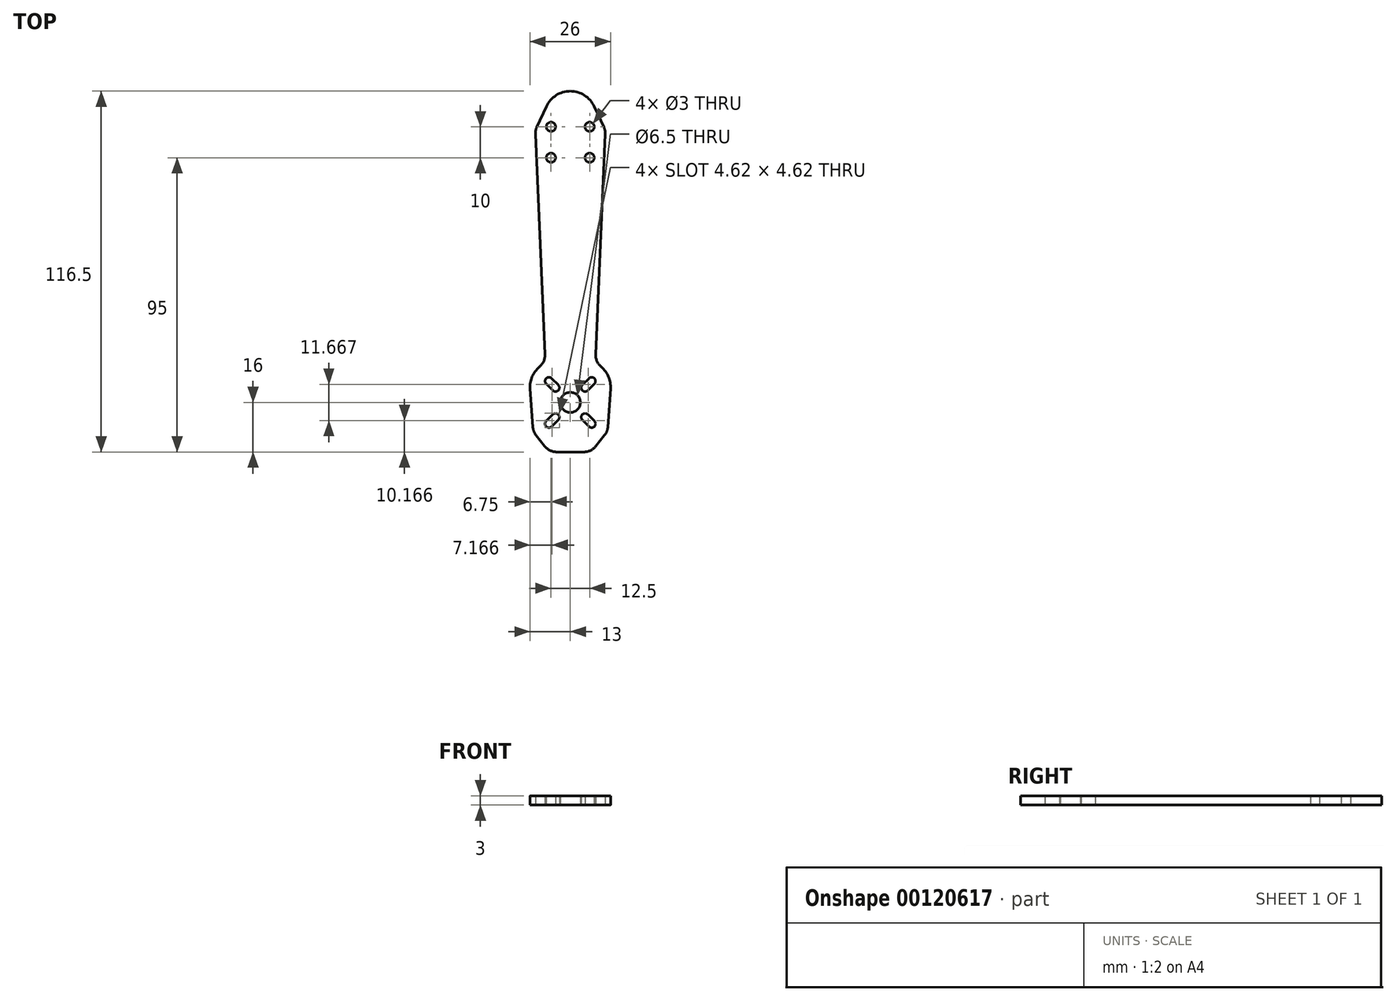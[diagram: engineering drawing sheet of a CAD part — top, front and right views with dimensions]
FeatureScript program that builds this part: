
annotation { "Feature Type Name" : "Feature", "Feature Type Description" : "" }
export const myFeature = defineFeature(function(context is Context, id is Id, definition is map)
    precondition{}
    {
        {
            var Q0;
            Q0=qCreatedBy(makeId("Top.planeOp"),FACE);
            var sketch = newSketch(context, id + "F0", { "sketchPlane" : qUnion([Q0])});
            skLineSegment(sketch, "E0", {"start": v(-6.01, -50.03) * mm, "end": v(-3.89, -47.9) * mm});
            skArc(sketch, "E1", {"start": v(-7.78, -48.26) * mm, "mid": v(-7.78, -50.03) * mm, "end": v(-6.01, -50.03) * mm});
            skArc(sketch, "E2", {"start": v(5.66, -46.14) * mm, "mid": v(3.89, -46.14) * mm, "end": v(3.89, -47.9) * mm});
            skArc(sketch, "E3", {"start": v(3.89, -36.6) * mm, "mid": v(3.89, -38.36) * mm, "end": v(5.66, -38.36) * mm});
            skArc(sketch, "E4", {"start": v(-6.01, -34.47) * mm, "mid": v(-7.78, -34.47) * mm, "end": v(-7.78, -36.24) * mm});
            skArc(sketch, "E5", {"start": v(11.28, 44.33) * mm, "mid": v(11.2, 45.52) * mm, "end": v(10.82, 46.66) * mm});
            skArc(sketch, "E6", {"start": v(12.98, -37.84) * mm, "mid": v(12.32, -33.93) * mm, "end": v(9.96, -30.74) * mm});
            skArc(sketch, "E7", {"start": v(-9.96, -30.74) * mm, "mid": v(-8.6, -28.92) * mm, "end": v(-8.18, -26.69) * mm});
            skArc(sketch, "E8", {"start": v(-9.96, -30.74) * mm, "mid": v(-12.32, -33.93) * mm, "end": v(-12.98, -37.84) * mm});
            skArc(sketch, "E9", {"start": v(8.18, -26.69) * mm, "mid": v(8.6, -28.92) * mm, "end": v(9.96, -30.74) * mm});
            skArc(sketch, "E10", {"start": v(-10.82, 46.66) * mm, "mid": v(-11.2, 45.52) * mm, "end": v(-11.28, 44.33) * mm});
            skCircle(sketch, "E11", {"center": v(0, -42.25) * mm, "radius": 3.25 * mm});
            skCircle(sketch, "E12", {"center": v(-6.25, 46.75) * mm, "radius": 1.5 * mm});
            skCircle(sketch, "E13", {"center": v(-6.25, 36.75) * mm, "radius": 1.5 * mm});
            skCircle(sketch, "E14", {"center": v(6.25, 46.75) * mm, "radius": 1.5 * mm});
            skCircle(sketch, "E15", {"center": v(6.25, 36.75) * mm, "radius": 1.5 * mm});
            skArc(sketch, "E16", {"start": v(-5.66, -38.36) * mm, "mid": v(-3.89, -38.36) * mm, "end": v(-3.89, -36.6) * mm});
            skArc(sketch, "E17", {"start": v(7.78, -36.24) * mm, "mid": v(7.78, -34.47) * mm, "end": v(6.01, -34.47) * mm});
            skArc(sketch, "E18", {"start": v(6.01, -50.03) * mm, "mid": v(7.78, -50.03) * mm, "end": v(7.78, -48.26) * mm});
            skArc(sketch, "E19", {"start": v(-3.89, -47.9) * mm, "mid": v(-3.89, -46.14) * mm, "end": v(-5.66, -46.14) * mm});
            skLineSegment(sketch, "E20", {"start": v(-11.28, 44.33) * mm, "end": v(-8.18, -26.69) * mm});
            skLineSegment(sketch, "E21", {"start": v(-12.98, -37.84) * mm, "end": v(-12.12, -50.1) * mm});
            skArc(sketch, "E22", {"start": v(-12.12, -50.1) * mm, "mid": v(-11.8, -51.56) * mm, "end": v(-11.05, -52.86) * mm});
            skLineSegment(sketch, "E23", {"start": v(-11.05, -52.86) * mm, "end": v(-8.26, -56.36) * mm});
            skArc(sketch, "E24", {"start": v(-8.26, -56.36) * mm, "mid": v(-6.52, -57.75) * mm, "end": v(-4.35, -58.25) * mm});
            skLineSegment(sketch, "E25", {"start": v(-4.35, -58.25) * mm, "end": v(4.35, -58.25) * mm});
            skArc(sketch, "E26", {"start": v(4.35, -58.25) * mm, "mid": v(6.52, -57.75) * mm, "end": v(8.26, -56.36) * mm});
            skLineSegment(sketch, "E27", {"start": v(8.26, -56.36) * mm, "end": v(11.05, -52.86) * mm});
            skArc(sketch, "E28", {"start": v(11.05, -52.86) * mm, "mid": v(11.8, -51.56) * mm, "end": v(12.12, -50.1) * mm});
            skLineSegment(sketch, "E29", {"start": v(12.12, -50.1) * mm, "end": v(12.98, -37.84) * mm});
            skLineSegment(sketch, "E30", {"start": v(8.18, -26.69) * mm, "end": v(11.28, 44.33) * mm});
            skLineSegment(sketch, "E31", {"start": v(10.82, 46.66) * mm, "end": v(7.7, 53.34) * mm});
            skArc(sketch, "E32", {"start": v(7.7, 53.34) * mm, "mid": v(0, 58.25) * mm, "end": v(-7.7, 53.34) * mm});
            skLineSegment(sketch, "E33", {"start": v(-7.7, 53.34) * mm, "end": v(-10.82, 46.66) * mm});
            skLineSegment(sketch, "E34", {"start": v(-5.66, -46.14) * mm, "end": v(-7.78, -48.26) * mm});
            skLineSegment(sketch, "E35", {"start": v(7.78, -48.26) * mm, "end": v(5.66, -46.14) * mm});
            skLineSegment(sketch, "E36", {"start": v(3.89, -47.9) * mm, "end": v(6.01, -50.03) * mm});
            skLineSegment(sketch, "E37", {"start": v(5.66, -38.36) * mm, "end": v(7.78, -36.24) * mm});
            skLineSegment(sketch, "E38", {"start": v(6.01, -34.47) * mm, "end": v(3.89, -36.6) * mm});
            skLineSegment(sketch, "E39", {"start": v(-3.89, -36.6) * mm, "end": v(-6.01, -34.47) * mm});
            skLineSegment(sketch, "E40", {"start": v(-7.78, -36.24) * mm, "end": v(-5.66, -38.36) * mm});
            skLineSegment(sketch, "E41", {"start": v(-6.25, 36.75) * mm, "end": v(6.25, 46.75) * mm, "construction": true});
            skLineSegment(sketch, "E42", {"start": v(6.25, 36.75) * mm, "end": v(-6.25, 46.75) * mm, "construction": true});
            skPoint(sketch, "E43", {"position": v(0, 41.75) * mm});
            skSolve(sketch);
        }
        {
            var Q0;
            Q0=makeQuery(id+"F0.imprint","IMPRINT",FACE,{"disambiguationData":[TD([[makeQuery(id+"F0.imprint","IMPRINT",EDGE,{"derivedFrom":sQuery(id+"F0.wireOp",EDGE,"E0")}),-1.0]])]});
            extrude(context, id + "F1", {"entities" : qUnion([Q0]), "depth" : 3 * mm});
        }
    });
